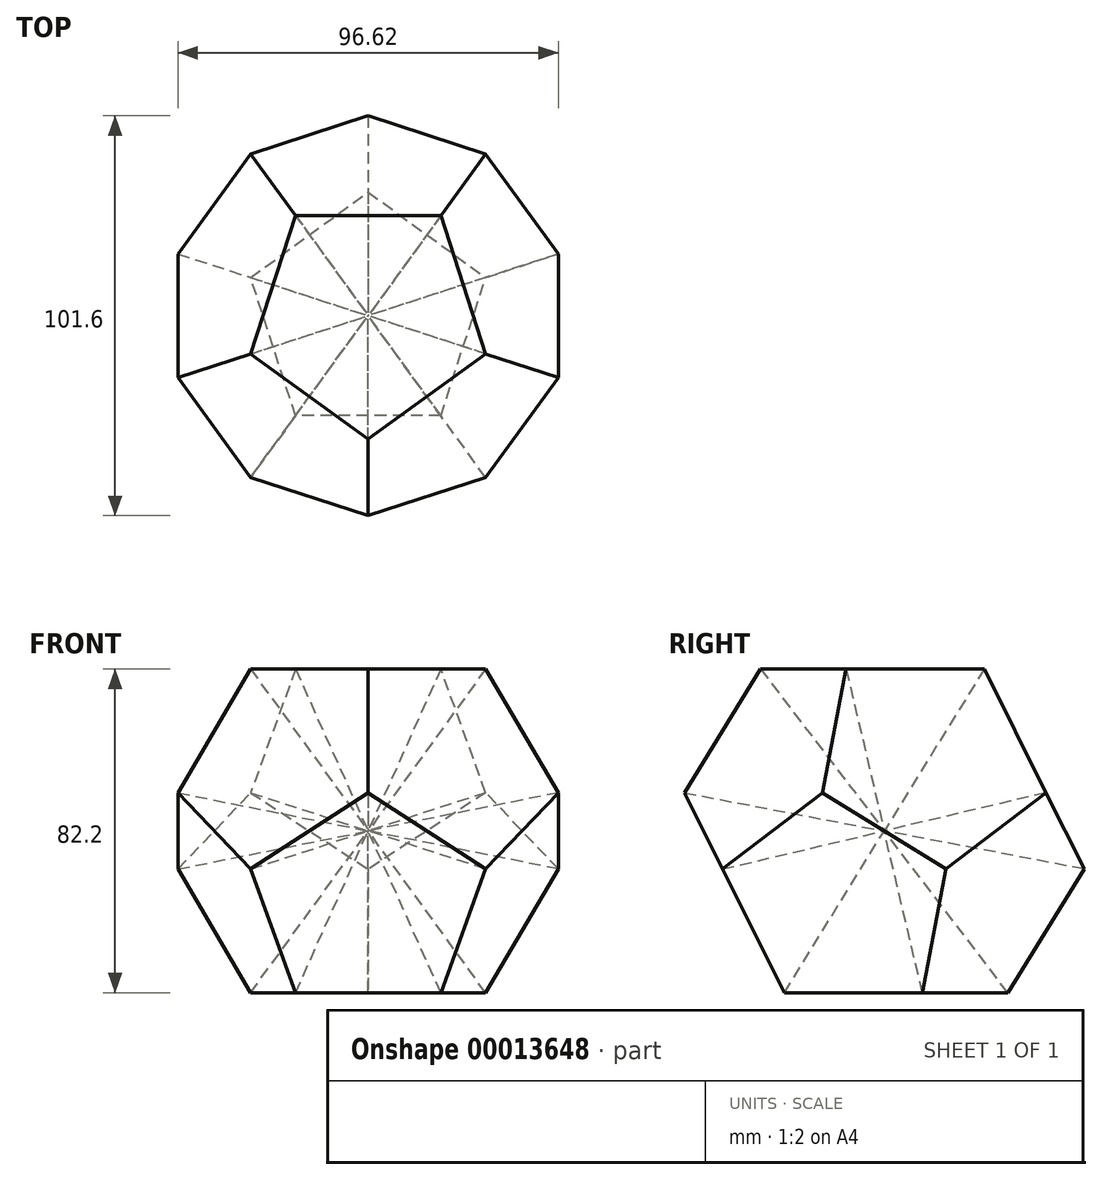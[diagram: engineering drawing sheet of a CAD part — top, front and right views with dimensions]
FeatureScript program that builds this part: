
annotation { "Feature Type Name" : "Feature", "Feature Type Description" : "" }
export const myFeature = defineFeature(function(context is Context, id is Id, definition is map)
    precondition{}
    {
        {
            var Q0;
            Q0=qCreatedBy(makeId("Top.planeOp"),FACE);
            var sketch = newSketch(context, id + "F0", { "sketchPlane" : qUnion([Q0])});
            skCircle(sketch, "E0.cCircle", {"center": v(0, 0) * mm, "radius": 25.4 * mm, "construction": true});
            skLineSegment(sketch, "E0.0", {"start": v(18.45, -25.4) * mm, "end": v(-18.45, -25.4) * mm});
            skLineSegment(sketch, "E0.1", {"start": v(-18.45, -25.4) * mm, "end": v(-29.86, 9.7) * mm});
            skLineSegment(sketch, "E0.2", {"start": v(-29.86, 9.7) * mm, "end": v(0, 31.4) * mm});
            skLineSegment(sketch, "E0.3", {"start": v(0, 31.4) * mm, "end": v(29.86, 9.7) * mm});
            skLineSegment(sketch, "E0.4", {"start": v(29.86, 9.7) * mm, "end": v(18.45, -25.4) * mm});
            skPoint(sketch, "E0.0.midPoint", {"position": v(0, -25.4) * mm});
            skLineSegment(sketch, "E1", {"start": v(18.45, -25.4) * mm, "end": v(0, -82.2) * mm, "construction": true});
            skLineSegment(sketch, "E2", {"start": v(0, -82.2) * mm, "end": v(-18.45, -25.4) * mm, "construction": true});
            skSolve(sketch);
        }
        {
            var Q0;
            Q0=qCreatedBy(makeId("Right.planeOp"),FACE);
            var sketch = newSketch(context, id + "F1", { "sketchPlane" : qUnion([Q0])});
            skLineSegment(sketch, "E3.0", {"start": v(-25.4, 0) * mm, "end": v(0, 0) * mm, "construction": true});
            skLineSegment(sketch, "E4", {"start": v(0, 0) * mm, "end": v(25.4, 0) * mm, "construction": true});
            skPoint(sketch, "E5.0", {"position": v(-82.2, 0) * mm});
            skLineSegment(sketch, "E6", {"start": v(-82.2, 0) * mm, "end": v(0, 41.1) * mm, "construction": true});
            skLineSegment(sketch, "E7", {"start": v(0, 41.1) * mm, "end": v(0, 0) * mm, "construction": true});
            skLineSegment(sketch, "E8", {"start": v(-25.4, 0) * mm, "end": v(-36.76, 22.72) * mm, "construction": true});
            skSolve(sketch);
        }
        {
            var Q0;
            Q0=makeQuery(id+"F0.imprint","IMPRINT",FACE,{"disambiguationData":[TD([[makeQuery(id+"F0.imprint","IMPRINT",EDGE,{"derivedFrom":sQuery(id+"F0.wireOp",EDGE,"E0.0")}),-1.0]])]});
            var Q1;
            Q1=sQuery(id+"F1.wireOp",VERTEX,"E6.end");
            loft(context, id + "F2", {"sheetProfilesArray" : [{ "sheetProfileEntities" : qUnion([Q0]) }, { "sheetProfileEntities" : qUnion([Q1]) }]});
        }
        {
            var Q0;
            Q0=makeQuery(id+"F2.opLoft","SWEPT_BODY",BODY,{"disambiguationData":[OSD([makeQuery(id+"F0.imprint","IMPRINT",FACE,{"disambiguationData":[TD([[makeQuery(id+"F0.imprint","IMPRINT",EDGE,{"derivedFrom":sQuery(id+"F0.wireOp",EDGE,"E0.0")}),-1.0]])]})])]});
            var Q1;
            Q1=sQuery(id+"F1.wireOp",EDGE,"E6");
            circularPattern(context, id + "F3", {"entities" : qUnion([Q0]), "axis" : qUnion([Q1]), "angle" : 360 * degree, "instanceCount" : round(5), "equalSpace" : true});
        }
        {
            var Q0;
            Q0=makeQuery(id+"F2.opLoft","SWEPT_BODY",BODY,{"disambiguationData":[OSD([makeQuery(id+"F0.imprint","IMPRINT",FACE,{"disambiguationData":[TD([[makeQuery(id+"F0.imprint","IMPRINT",EDGE,{"derivedFrom":sQuery(id+"F0.wireOp",EDGE,"E0.0")}),-1.0]])]})])]});
            var Q1;
            Q1=makeQuery(id+"F3.opPattern","COPY",BODY,{"derivedFrom":makeQuery(id+"F2.opLoft","SWEPT_BODY",BODY,{"disambiguationData":[OSD([makeQuery(id+"F0.imprint","IMPRINT",FACE,{"disambiguationData":[TD([[makeQuery(id+"F0.imprint","IMPRINT",EDGE,{"derivedFrom":sQuery(id+"F0.wireOp",EDGE,"E0.0")}),-1.0]])]})])]}),"instanceName":"2"});
            var Q2;
            Q2=makeQuery(id+"F3.opPattern","COPY",BODY,{"derivedFrom":makeQuery(id+"F2.opLoft","SWEPT_BODY",BODY,{"disambiguationData":[OSD([makeQuery(id+"F0.imprint","IMPRINT",FACE,{"disambiguationData":[TD([[makeQuery(id+"F0.imprint","IMPRINT",EDGE,{"derivedFrom":sQuery(id+"F0.wireOp",EDGE,"E0.0")}),-1.0]])]})])]}),"instanceName":"1"});
            var Q3;
            Q3=makeQuery(id+"F2.opLoft","SWEPT_FACE",FACE,{"disambiguationData":[OSD([sQuery(id+"F0.wireOp",EDGE,"E0.2"),sQuery(id+"F0.wireOp",EDGE,"E0.3"),sQuery(id+"F0.wireOp",EDGE,"E0.4")])]});
            mirror(context, id + "F4", {"entities" : qUnion([Q0, Q1, Q2]), "mirrorPlane" : qUnion([Q3])});
        }
        {
            var Q0;
            Q0=makeQuery(id+"F4.opPattern","COPY",BODY,{"derivedFrom":makeQuery(id+"F3.opPattern","COPY",BODY,{"derivedFrom":makeQuery(id+"F2.opLoft","SWEPT_BODY",BODY,{"disambiguationData":[OSD([makeQuery(id+"F0.imprint","IMPRINT",FACE,{"disambiguationData":[TD([[makeQuery(id+"F0.imprint","IMPRINT",EDGE,{"derivedFrom":sQuery(id+"F0.wireOp",EDGE,"E0.0")}),-1.0]])]})])]}),"instanceName":"1"}),"instanceName":"1"});
            var Q1;
            Q1=makeQuery(id+"F3.opPattern","COPY",BODY,{"derivedFrom":makeQuery(id+"F2.opLoft","SWEPT_BODY",BODY,{"disambiguationData":[OSD([makeQuery(id+"F0.imprint","IMPRINT",FACE,{"disambiguationData":[TD([[makeQuery(id+"F0.imprint","IMPRINT",EDGE,{"derivedFrom":sQuery(id+"F0.wireOp",EDGE,"E0.0")}),-1.0]])]})])]}),"instanceName":"3"});
            var Q2;
            Q2=makeQuery(id+"F3.opPattern","COPY",BODY,{"derivedFrom":makeQuery(id+"F2.opLoft","SWEPT_BODY",BODY,{"disambiguationData":[OSD([makeQuery(id+"F0.imprint","IMPRINT",FACE,{"disambiguationData":[TD([[makeQuery(id+"F0.imprint","IMPRINT",EDGE,{"derivedFrom":sQuery(id+"F0.wireOp",EDGE,"E0.0")}),-1.0]])]})])]}),"instanceName":"4"});
            var Q3;
            Q3=makeQuery(id+"F3.opPattern","COPY",BODY,{"derivedFrom":makeQuery(id+"F2.opLoft","SWEPT_BODY",BODY,{"disambiguationData":[OSD([makeQuery(id+"F0.imprint","IMPRINT",FACE,{"disambiguationData":[TD([[makeQuery(id+"F0.imprint","IMPRINT",EDGE,{"derivedFrom":sQuery(id+"F0.wireOp",EDGE,"E0.0")}),-1.0]])]})])]}),"instanceName":"1"});
            var Q4;
            Q4=makeQuery(id+"F4.opPattern","COPY",FACE,{"derivedFrom":makeQuery(id+"F3.opPattern","COPY",FACE,{"derivedFrom":makeQuery(id+"F2.opLoft","SWEPT_FACE",FACE,{"disambiguationData":[OSD([sQuery(id+"F0.wireOp",EDGE,"E0.0"),sQuery(id+"F0.wireOp",EDGE,"E0.1"),sQuery(id+"F0.wireOp",EDGE,"E0.4")])]}),"instanceName":"1"}),"instanceName":"1"});
            mirror(context, id + "F5", {"entities" : qUnion([Q0, Q1, Q2, Q3]), "mirrorPlane" : qUnion([Q4])});
        }
    });
